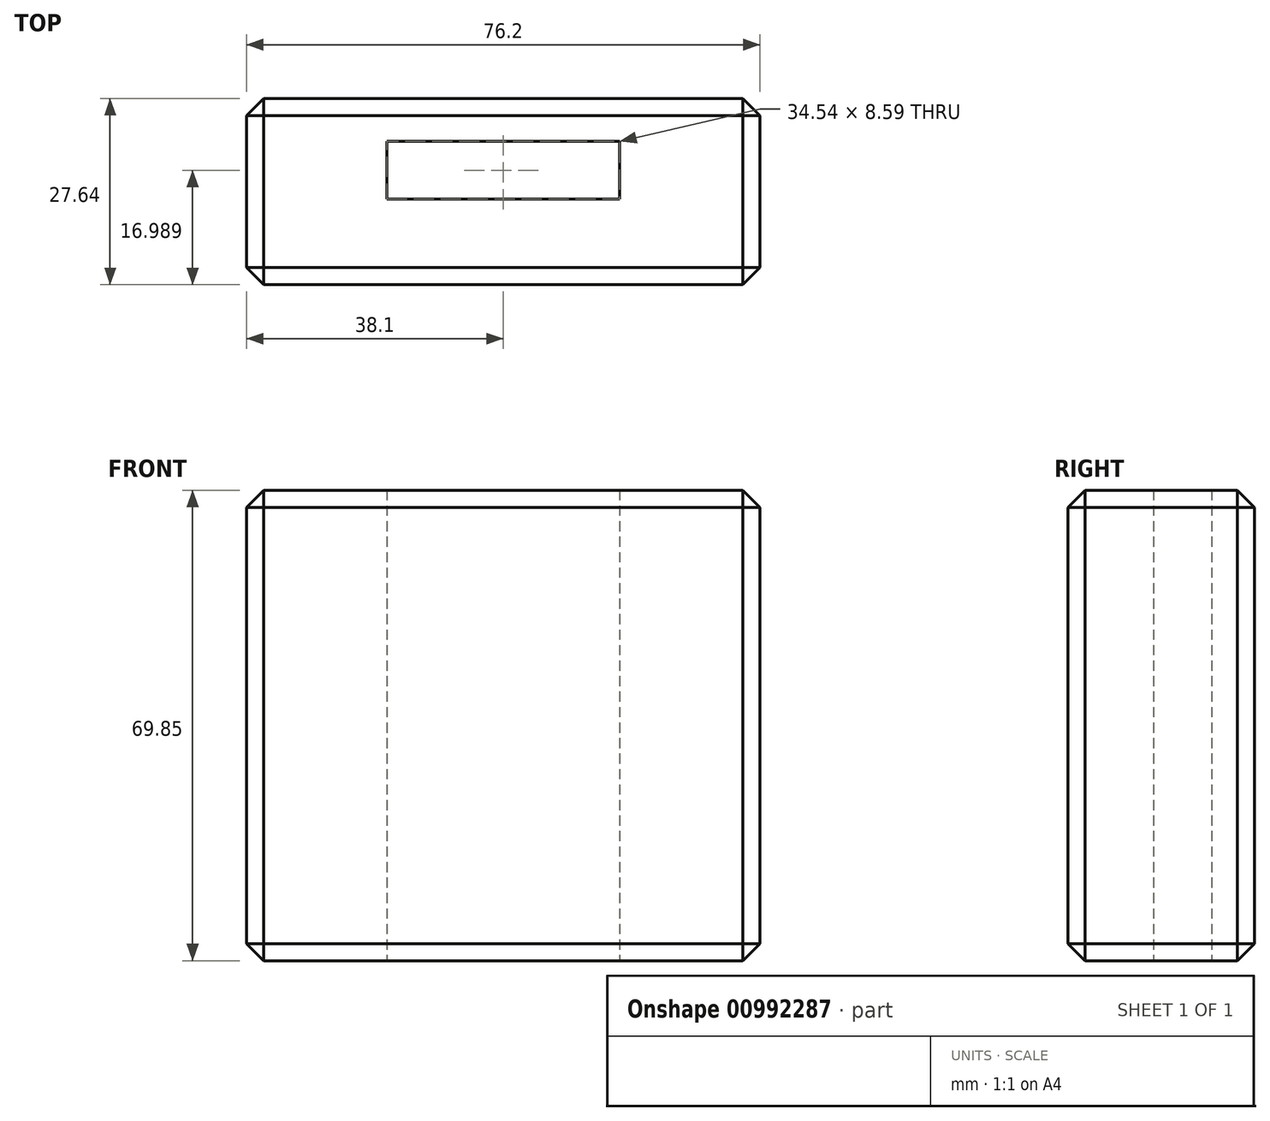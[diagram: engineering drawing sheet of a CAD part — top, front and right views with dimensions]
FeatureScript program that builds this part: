
annotation { "Feature Type Name" : "Feature", "Feature Type Description" : "" }
export const myFeature = defineFeature(function(context is Context, id is Id, definition is map)
    precondition{}
    {
        {
            var Q0;
            Q0=qCreatedBy(makeId("Top.planeOp"),FACE);
            var sketch = newSketch(context, id + "F0", { "sketchPlane" : qUnion([Q0])});
            skLineSegment(sketch, "E0.bottom", {"start": v(38.1, -13.82) * mm, "end": v(-38.1, -13.82) * mm});
            skLineSegment(sketch, "E0.top", {"start": v(38.1, 13.82) * mm, "end": v(-38.1, 13.82) * mm});
            skLineSegment(sketch, "E0.left", {"start": v(38.1, -13.82) * mm, "end": v(38.1, 13.82) * mm});
            skLineSegment(sketch, "E0.right", {"start": v(-38.1, -13.82) * mm, "end": v(-38.1, 13.82) * mm});
            skPoint(sketch, "E0.middle", {"position": v(0, 0) * mm});
            skLineSegment(sketch, "E1", {"start": v(-17.27, -1.12) * mm, "end": v(-17.27, -13.82) * mm, "construction": true});
            skLineSegment(sketch, "E2", {"start": v(-17.27, -1.12) * mm, "end": v(-38.1, -1.12) * mm, "construction": true});
            skLineSegment(sketch, "E3.bottom", {"start": v(-17.27, -1.12) * mm, "end": v(17.27, -1.12) * mm});
            skLineSegment(sketch, "E3.top", {"start": v(-17.27, 7.46) * mm, "end": v(17.27, 7.46) * mm});
            skLineSegment(sketch, "E3.left", {"start": v(-17.27, -1.12) * mm, "end": v(-17.27, 7.46) * mm});
            skLineSegment(sketch, "E3.right", {"start": v(17.27, -1.12) * mm, "end": v(17.27, 7.46) * mm});
            skSolve(sketch);
        }
        {
            var Q0;
            Q0 = qSketchRegion(id + "F0", true);
            extrude(context, id + "F1", {"entities" : qUnion([Q0]), "depth" : 69.85 * mm, "offsetDistance" : 25.4 * mm});
        }
        {
            var Q0;
            Q0=makeQuery(id+"F1.opExtrude","SWEPT_EDGE",EDGE,{"disambiguationData":[OSD([sQuery(id+"F0.wireOp",EDGE,"E0.bottom"),sQuery(id+"F0.wireOp",EDGE,"E0.left")])]});
            var Q1;
            Q1=makeQuery(id+"F1.opExtrude","SWEPT_EDGE",EDGE,{"disambiguationData":[OSD([sQuery(id+"F0.wireOp",EDGE,"E0.bottom"),sQuery(id+"F0.wireOp",EDGE,"E0.right")])]});
            var Q2;
            Q2=makeQuery(id+"F1.opExtrude","SWEPT_EDGE",EDGE,{"disambiguationData":[OSD([sQuery(id+"F0.wireOp",EDGE,"E0.top"),sQuery(id+"F0.wireOp",EDGE,"E0.left")])]});
            var Q3;
            Q3=makeQuery(id+"F1.opExtrude","SWEPT_EDGE",EDGE,{"disambiguationData":[OSD([sQuery(id+"F0.wireOp",EDGE,"E0.top"),sQuery(id+"F0.wireOp",EDGE,"E0.right")])]});
            var Q4;
            Q4=makeQuery(id+"F1.opExtrude","CAP_EDGE",EDGE,{"disambiguationData":[OSD([sQuery(id+"F0.wireOp",EDGE,"E0.top")])],"isStart":false});
            var Q5;
            Q5=makeQuery(id+"F1.opExtrude","CAP_EDGE",EDGE,{"disambiguationData":[OSD([sQuery(id+"F0.wireOp",EDGE,"E0.bottom")])],"isStart":false});
            var Q6;
            Q6=makeQuery(id+"F1.opExtrude","CAP_EDGE",EDGE,{"disambiguationData":[OSD([sQuery(id+"F0.wireOp",EDGE,"E0.bottom")])],"isStart":true});
            var Q7;
            Q7=makeQuery(id+"F1.opExtrude","CAP_EDGE",EDGE,{"disambiguationData":[OSD([sQuery(id+"F0.wireOp",EDGE,"E0.top")])],"isStart":true});
            var Q8;
            Q8=makeQuery(id+"F1.opExtrude","CAP_EDGE",EDGE,{"disambiguationData":[OSD([sQuery(id+"F0.wireOp",EDGE,"E0.right")])],"isStart":true});
            var Q9;
            Q9=makeQuery(id+"F1.opExtrude","CAP_EDGE",EDGE,{"disambiguationData":[OSD([sQuery(id+"F0.wireOp",EDGE,"E0.left")])],"isStart":true});
            var Q10;
            Q10=makeQuery(id+"F1.opExtrude","CAP_EDGE",EDGE,{"disambiguationData":[OSD([sQuery(id+"F0.wireOp",EDGE,"E0.left")])],"isStart":false});
            var Q11;
            Q11=makeQuery(id+"F1.opExtrude","CAP_EDGE",EDGE,{"disambiguationData":[OSD([sQuery(id+"F0.wireOp",EDGE,"E0.right")])],"isStart":false});
            chamfer(context, id + "F2", {"entities" : qUnion([Q0, Q1, Q2, Q3, Q4, Q5, Q6, Q7, Q8, Q9, Q10, Q11]), "width" : 2.54 * mm, "tangentPropagation" : true});
        }
    });
